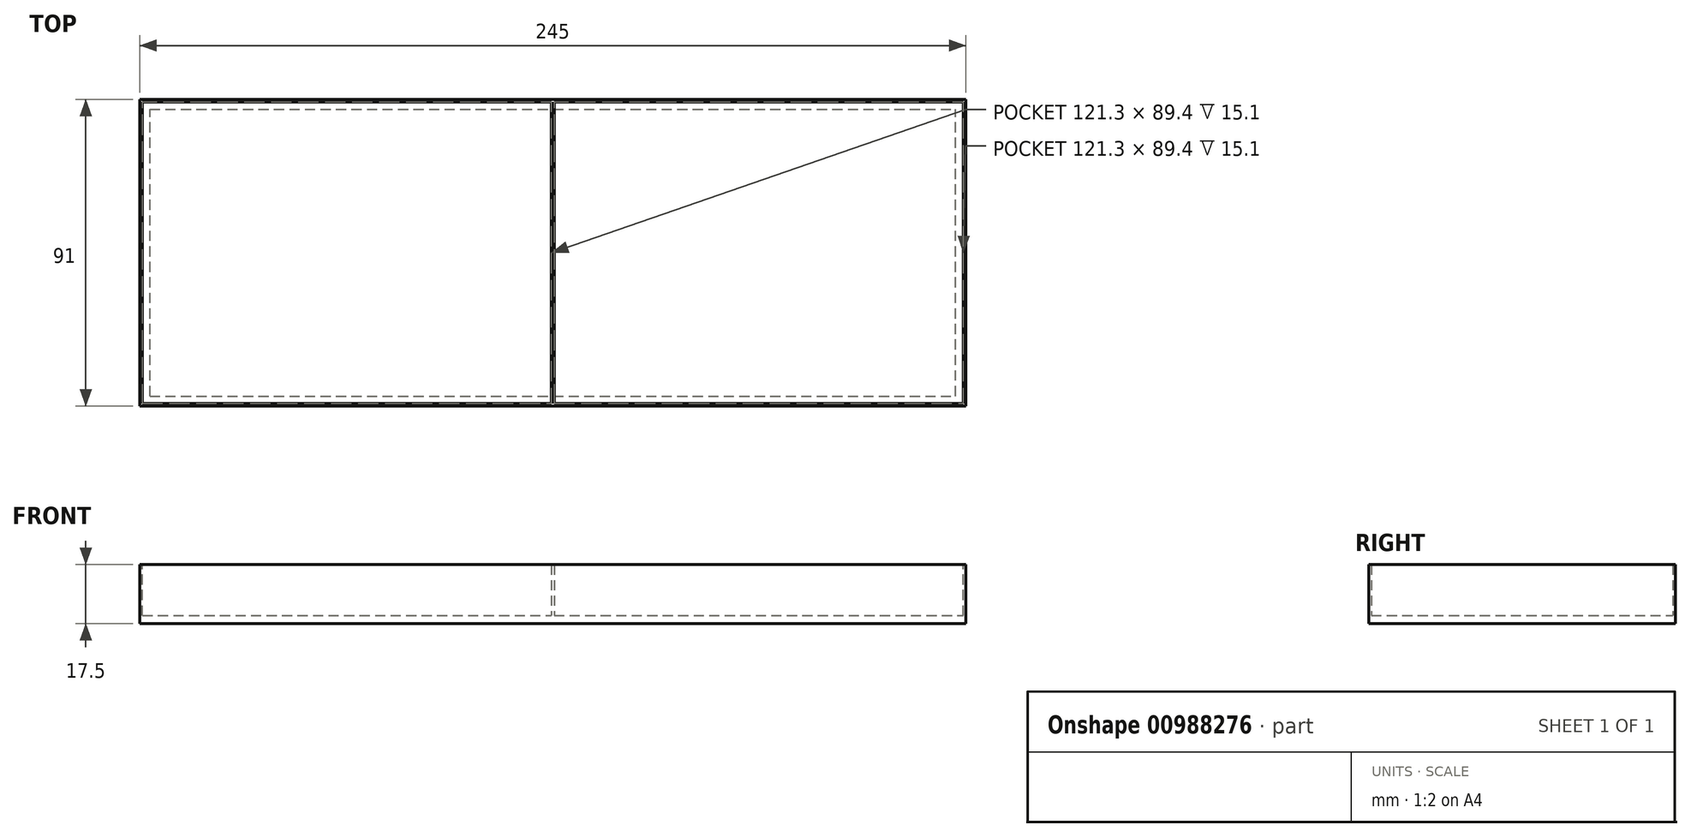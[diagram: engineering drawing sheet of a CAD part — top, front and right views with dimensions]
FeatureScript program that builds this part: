
annotation { "Feature Type Name" : "Feature", "Feature Type Description" : "" }
export const myFeature = defineFeature(function(context is Context, id is Id, definition is map)
    precondition{}
    {
        {
            var Q0;
            Q0=qCreatedBy(makeId("Top.planeOp"),FACE);
            var sketch = newSketch(context, id + "F0", { "sketchPlane" : qUnion([Q0])});
            skLineSegment(sketch, "E0.bottom", {"start": v(-122.5, -45.5) * mm, "end": v(122.5, -45.5) * mm});
            skLineSegment(sketch, "E0.top", {"start": v(-122.5, 45.5) * mm, "end": v(122.5, 45.5) * mm});
            skLineSegment(sketch, "E0.left", {"start": v(-122.5, -45.5) * mm, "end": v(-122.5, 45.5) * mm});
            skLineSegment(sketch, "E0.right", {"start": v(122.5, -45.5) * mm, "end": v(122.5, 45.5) * mm});
            skPoint(sketch, "E0.middle", {"position": v(0, 0) * mm});
            skSolve(sketch);
        }
        {
            var Q0;
            Q0=makeQuery(id+"F0.imprint","IMPRINT",FACE,{"disambiguationData":[TD([[makeQuery(id+"F0.imprint","IMPRINT",EDGE,{"derivedFrom":sQuery(id+"F0.wireOp",EDGE,"E0.bottom")}),1.0]])]});
            extrude(context, id + "F1", {"entities" : qUnion([Q0]), "depth" : 17.5 * mm, "offsetDistance" : 25 * mm});
        }
        {
            var Q0;
            Q0=makeQuery(id+"F1.opExtrude","CAP_FACE",FACE,{"disambiguationData":[OSD([sQuery(id+"F0.wireOp",EDGE,"E0.bottom"),sQuery(id+"F0.wireOp",EDGE,"E0.top"),sQuery(id+"F0.wireOp",EDGE,"E0.left"),sQuery(id+"F0.wireOp",EDGE,"E0.right")])],"isStart":false});
            var sketch = newSketch(context, id + "F2", { "sketchPlane" : qUnion([Q0])});
            skLineSegment(sketch, "E1.bottom", {"start": v(-121.7, -44.7) * mm, "end": v(121.7, -44.7) * mm});
            skLineSegment(sketch, "E1.top", {"start": v(-121.7, 44.7) * mm, "end": v(121.7, 44.7) * mm});
            skLineSegment(sketch, "E1.left", {"start": v(-121.7, -44.7) * mm, "end": v(-121.7, 44.7) * mm});
            skLineSegment(sketch, "E1.right", {"start": v(121.7, -44.7) * mm, "end": v(121.7, 44.7) * mm});
            skPoint(sketch, "E1.middle", {"position": v(0, 0) * mm});
            skSolve(sketch);
        }
        {
            var Q0;
            Q0=makeQuery(id+"F2.imprint","IMPRINT",FACE,{"disambiguationData":[TD([[makeQuery(id+"F2.imprint","IMPRINT",EDGE,{"derivedFrom":sQuery(id+"F2.wireOp",EDGE,"E1.bottom")}),1.0]])]});
            extrude(context, id + "F3", {"entities" : qUnion([Q0]), "operationType" : NewBodyOperationType.REMOVE, "oppositeDirection" : true, "depth" : 15.1 * mm, "offsetDistance" : 25 * mm});
        }
        {
            var Q0;
            Q0=makeQuery(id+"F3.boolean.opBoolean","COPY",FACE,{"derivedFrom":makeQuery(id+"F3.opExtrude","CAP_FACE",FACE,{"disambiguationData":[OSD([sQuery(id+"F2.wireOp",EDGE,"E1.bottom"),sQuery(id+"F2.wireOp",EDGE,"E1.top"),sQuery(id+"F2.wireOp",EDGE,"E1.left"),sQuery(id+"F2.wireOp",EDGE,"E1.right")])],"isStart":false})});
            var sketch = newSketch(context, id + "F4", { "sketchPlane" : qUnion([Q0])});
            skLineSegment(sketch, "E2.bottom", {"start": v(-0.4, -44.7) * mm, "end": v(0.4, -44.7) * mm});
            skLineSegment(sketch, "E2.top", {"start": v(-0.4, 44.7) * mm, "end": v(0.4, 44.7) * mm});
            skLineSegment(sketch, "E2.left", {"start": v(-0.4, -44.7) * mm, "end": v(-0.4, 44.7) * mm});
            skLineSegment(sketch, "E2.right", {"start": v(0.4, -44.7) * mm, "end": v(0.4, 44.7) * mm});
            skPoint(sketch, "E2.middle", {"position": v(0, 0) * mm});
            skSolve(sketch);
        }
        {
            var Q0;
            Q0 = qSketchRegion(id + "F4", true);
            extrude(context, id + "F5", {"entities" : qUnion([Q0]), "operationType" : NewBodyOperationType.ADD, "depth" : 15.1 * mm, "offsetDistance" : 25 * mm});
        }
        {
            var Q0;
            Q0=makeQuery(id+"F1.opExtrude","CAP_FACE",FACE,{"disambiguationData":[OSD([sQuery(id+"F0.wireOp",EDGE,"E0.bottom"),sQuery(id+"F0.wireOp",EDGE,"E0.top"),sQuery(id+"F0.wireOp",EDGE,"E0.left"),sQuery(id+"F0.wireOp",EDGE,"E0.right")])],"isStart":true});
            var sketch = newSketch(context, id + "F6", { "sketchPlane" : qUnion([Q0])});
            skLineSegment(sketch, "E3.0", {"start": v(-119.5, -42.5) * mm, "end": v(119.5, -42.5) * mm});
            skLineSegment(sketch, "E3.1", {"start": v(-119.5, 42.5) * mm, "end": v(-119.5, -42.5) * mm});
            skLineSegment(sketch, "E3.2", {"start": v(-119.5, 42.5) * mm, "end": v(119.5, 42.5) * mm});
            skLineSegment(sketch, "E3.3", {"start": v(119.5, 42.5) * mm, "end": v(119.5, -42.5) * mm});
            skSolve(sketch);
        }
        {
            var Q0;
            Q0 = qSketchRegion(id + "F6", true);
            extrude(context, id + "F7", {"entities" : qUnion([Q0]), "operationType" : NewBodyOperationType.REMOVE, "oppositeDirection" : true, "depth" : .2 * mm, "offsetDistance" : 25 * mm});
        }
    });
